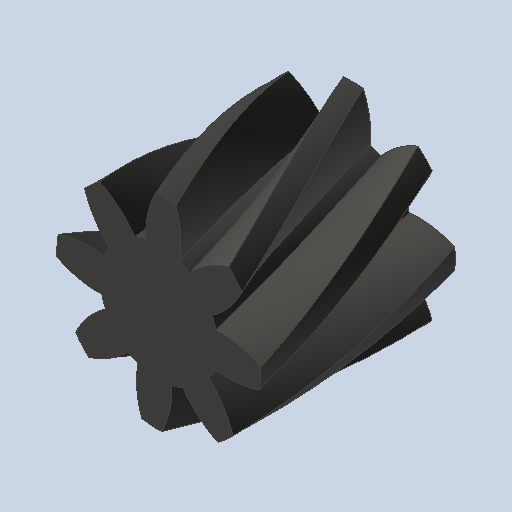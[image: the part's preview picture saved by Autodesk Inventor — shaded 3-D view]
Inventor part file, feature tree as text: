
AUTODESK INVENTOR PART (.ipt)
format: ipt  version: 2023 (Build 270158000, 158)  size: 305,664 bytes
history: native  units: mm (DEFAULTED — no unit token found)
features: plane x3, other x3, sketch x2, extrude x1
ambient origin geometry x8: Origin, YZ Plane, XZ Plane, XY Plane, X Axis, Y Axis, Z Axis, Center Point
bodies: Solid1 (feature_tree)
feature tree (9):
  extrude  "Extrusion1"  Depth=15.0mm TaperAngle=0.0deg
  plane  "Work Plane2"
  plane  "Work Plane8"
  plane  "Work Plane9"
  other  "Spur Gear"
  sketch  "Sketch1"  dims[d0=15.743465mm d1=15.0mm d2=0.0mm]
  sketch  "Sketch2"  dims[d3=12.770133mm d4=10.0mm d5=0.0mm d16=57.15mm d17=0.0mm d34=22.5deg d39=0.0mm d41=0.0mm d43=57.15mm d46=57.15mm d47=0.0mm d48=0.0mm]
  other  "Srf1"
  other  "Pitch Diameter"
